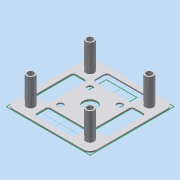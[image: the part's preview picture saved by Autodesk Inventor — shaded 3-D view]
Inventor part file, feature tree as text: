
AUTODESK INVENTOR PART (.ipt)
format: ipt  version: 2015 (Build 190159000, 159)  size: 201,728 bytes
history: native  units: in
note: dims shown in document units (in); Inventor stores cm internally (conversion verified against a paired STEP export)
features: other x4, plane x3, sketch x2, extrude x2, fillet x2
ambient origin geometry x2: Origin, Center Point
bodies: Body1 (feature_tree)
feature tree (13):
  other  "SensorMount_top.ipt"
  sketch  "Sketch3"  dims[d4=0.1693in d5=0.1693in d6=0.1693in d7=1.1811in d8=1.1811in d9=0.2362in d10=0.2362in d11=0.2362in d12=0.2362in d13=0.0394in d14=0.0in d15=0.8071in d16=0.0in d17=0.3937in d18=0.1969in d19=0.0787in]
  extrude  "Extrusion1"  Depth=0.3937in
  extrude  "Extrusion2"  Depth=0.0787in
  fillet  "Fillet1"  Radius=0.1693in
  fillet  "Fillet2"  Radius=1.1811in
  plane  "YZ Plane Vertical Spine"
  plane  "XZ Plane Horizontal"
  plane  "XY Plane Vertical Span"
  other  "X Axis Left/Right"
  other  "Y Axis Up/Down"
  other  "Z Axis Fore/Aft"
  sketch  "Sketch1"  dims[d2=0.3937in d3=0.1693in]
